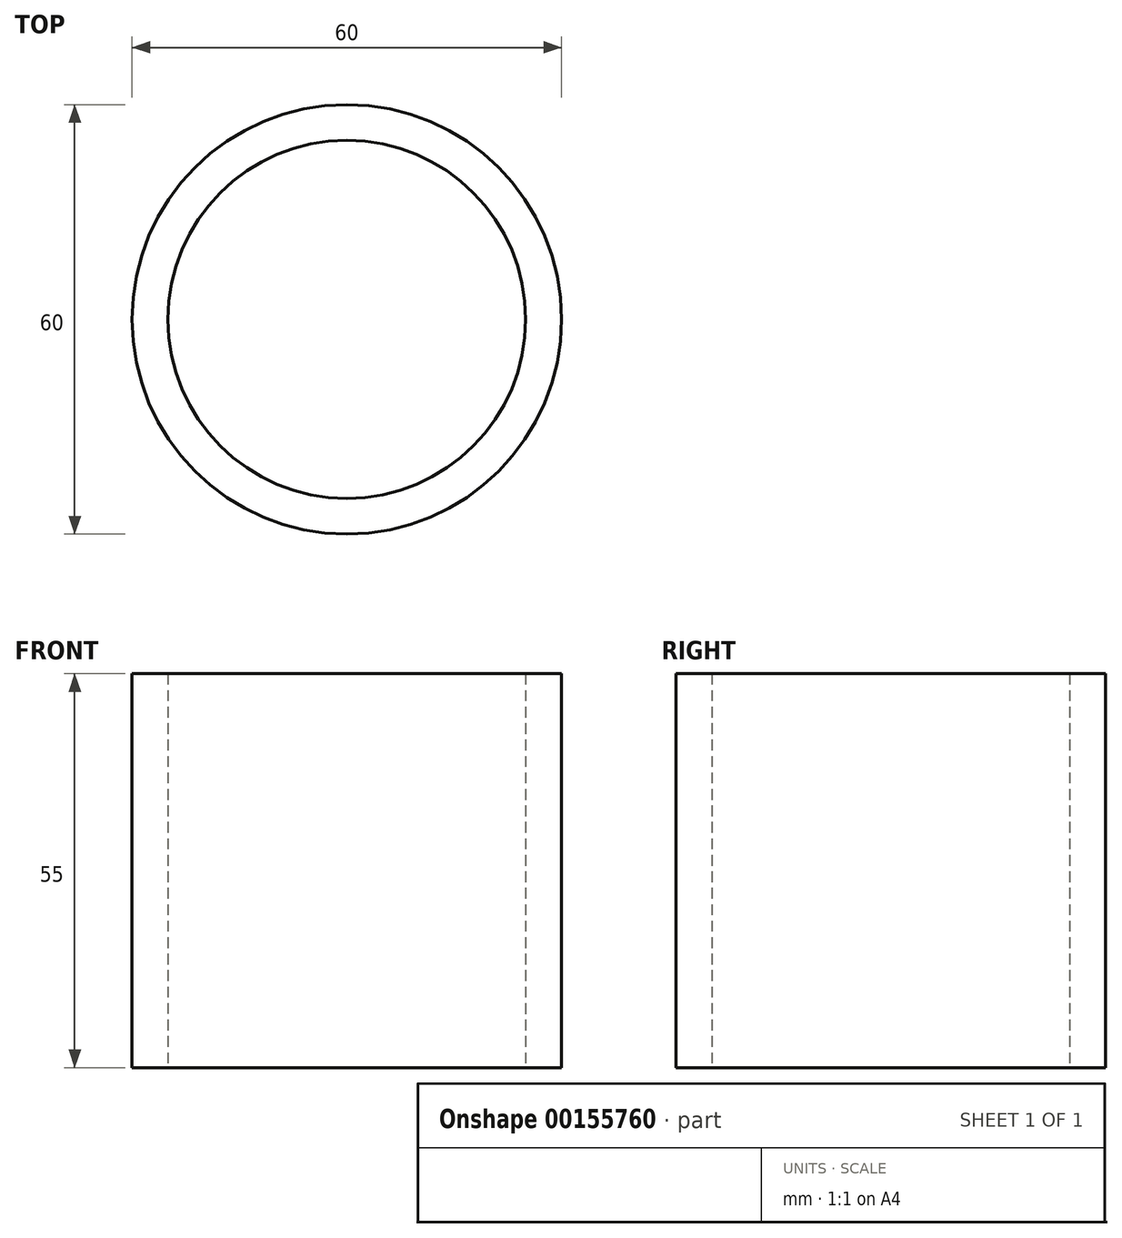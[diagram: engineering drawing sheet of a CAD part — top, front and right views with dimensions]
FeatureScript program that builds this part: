
annotation { "Feature Type Name" : "Feature", "Feature Type Description" : "" }
export const myFeature = defineFeature(function(context is Context, id is Id, definition is map)
    precondition{}
    {
        {
            assignVariable(context, id + "F0", {"name" : "shaft_h", "anyValue" : 55});
        }
        {
            var Q0;
            Q0=qCreatedBy(makeId("Top.planeOp"),FACE);
            var sketch = newSketch(context, id + "F1", { "sketchPlane" : qUnion([Q0])});
            skCircle(sketch, "E0", {"center": v(0, 0) * mm, "radius": 30 * mm});
            skCircle(sketch, "E1", {"center": v(0, 0) * mm, "radius": 25 * mm});
            skSolve(sketch);
        }
        {
            var Q0;
            Q0=makeQuery(id+"F1.imprint","IMPRINT",FACE,{"disambiguationData":[TD([[makeQuery(id+"F1.imprint","IMPRINT",EDGE,{"derivedFrom":sQuery(id+"F1.wireOp",EDGE,"E0")}),1.0]])]});
            extrude(context, id + "F2", {"entities" : qUnion([Q0]), "depth" : (getVariable(context, 'shaft_h')) * mm});
        }
    });
